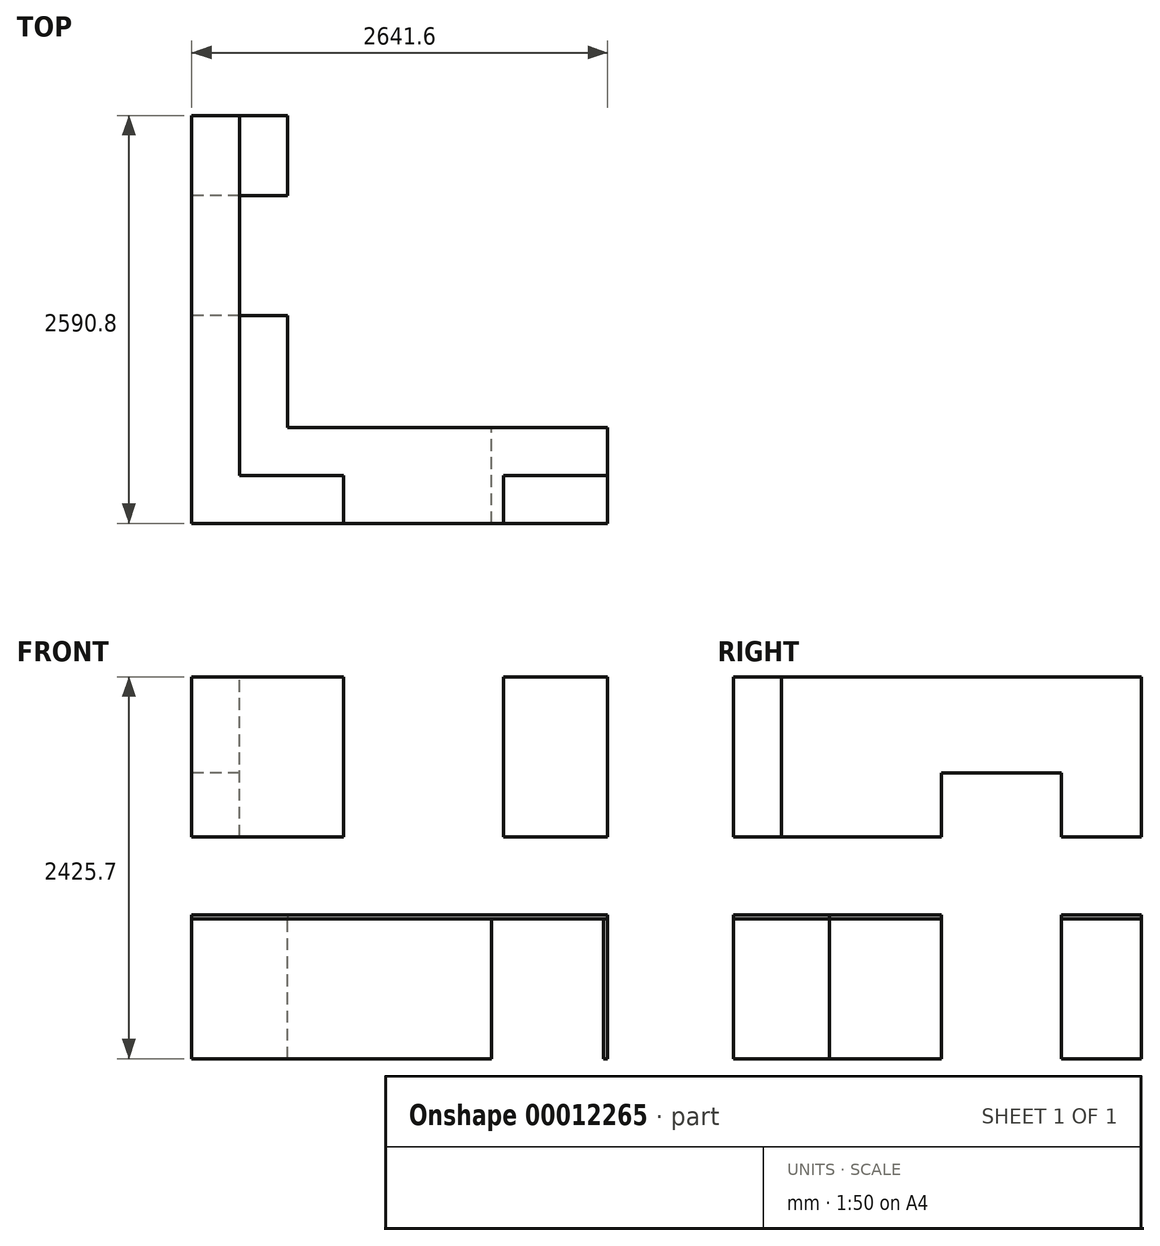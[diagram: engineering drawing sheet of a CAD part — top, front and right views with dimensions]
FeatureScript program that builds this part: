
annotation { "Feature Type Name" : "Feature", "Feature Type Description" : "" }
export const myFeature = defineFeature(function(context is Context, id is Id, definition is map)
    precondition{}
    {
        {
            var Q0;
            Q0=qCreatedBy(makeId("Top.planeOp"),FACE);
            cPlane(context, id + "F0", {"entities" : qUnion([Q0]), "cplaneType" : CPlaneType.OFFSET, "offset" : 889 * mm, "width" : 152.4 * mm, "height" : 152.4 * mm});
        }
        {
            var Q0;
            Q0=qCreatedBy(id+"F0.planeOp",FACE);
            cPlane(context, id + "F1", {"entities" : qUnion([Q0]), "cplaneType" : CPlaneType.OFFSET, "offset" : 25.4 * mm, "width" : 152.4 * mm, "height" : 152.4 * mm});
        }
        {
            var Q0;
            Q0=qCreatedBy(makeId("Top.planeOp"),FACE);
            cPlane(context, id + "F2", {"entities" : qUnion([Q0]), "cplaneType" : CPlaneType.OFFSET, "offset" : 2425.7 * mm, "width" : 152.4 * mm, "height" : 152.4 * mm});
        }
        {
            var Q0;
            Q0=qCreatedBy(id+"F0.planeOp",FACE);
            var sketch = newSketch(context, id + "F3", { "sketchPlane" : qUnion([Q0])});
            skLineSegment(sketch, "E0", {"start": v(0, 0) * mm, "end": v(0, 2590.8) * mm});
            skLineSegment(sketch, "E1", {"start": v(0, 0) * mm, "end": v(2641.6, 0) * mm});
            skLineSegment(sketch, "E2", {"start": v(0, 2590.8) * mm, "end": v(609.6, 2590.8) * mm});
            skLineSegment(sketch, "E3", {"start": v(609.6, 2590.8) * mm, "end": v(609.6, 609.6) * mm});
            skLineSegment(sketch, "E4", {"start": v(609.6, 609.6) * mm, "end": v(2641.6, 609.6) * mm});
            skLineSegment(sketch, "E5", {"start": v(2641.6, 609.6) * mm, "end": v(2641.6, 0) * mm});
            skLineSegment(sketch, "E6", {"start": v(2616.2, 609.6) * mm, "end": v(2616.2, 0) * mm});
            skLineSegment(sketch, "E7", {"start": v(1905, 609.6) * mm, "end": v(1905, 0) * mm});
            skLineSegment(sketch, "E8", {"start": v(609.6, 1320.8) * mm, "end": v(0, 1320.8) * mm});
            skLineSegment(sketch, "E9", {"start": v(609.6, 2082.8) * mm, "end": v(0, 2082.8) * mm});
            skSolve(sketch);
        }
        {
            var Q0;
            {var subQ1=sQuery(id+"F3.wireOp",EDGE,"E5");Q0=makeQuery(id+"F3.imprint","IMPRINT",FACE,{"disambiguationData":[TD([[makeQuery(id+"F3.imprint","IMPRINT",EDGE,{"derivedFrom":subQ1}),-1.0]])]});}
            var Q1;
            {var subQ1=sQuery(id+"F3.wireOp",EDGE,"E7");Q1=makeQuery(id+"F3.imprint","IMPRINT",FACE,{"disambiguationData":[TD([[makeQuery(id+"F3.imprint","IMPRINT",EDGE,{"derivedFrom":subQ1}),-1.0]])]});}
            var Q2;
            {var subQ2=sQuery(id+"F3.wireOp",EDGE,"E2");Q2=makeQuery(id+"F3.imprint","IMPRINT",FACE,{"disambiguationData":[TD([[makeQuery(id+"F3.imprint","IMPRINT",EDGE,{"derivedFrom":subQ2}),-1.0]])]});}
            var Q3;
            Q3=qCreatedBy(makeId("Top.planeOp"),FACE);
            extrude(context, id + "F4", {"entities" : qUnion([Q0, Q1, Q2]), "endBound" : BoundingType.UP_TO_SURFACE, "oppositeDirection" : true, "endBoundEntityFace" : qUnion([Q3]), "depth" : 25.4 * mm});
        }
        {
            var Q0;
            {var subQ1=sQuery(id+"F3.wireOp",EDGE,"E5");Q0=makeQuery(id+"F3.imprint","IMPRINT",FACE,{"disambiguationData":[TD([[makeQuery(id+"F3.imprint","IMPRINT",EDGE,{"derivedFrom":subQ1}),-1.0]])]});}
            var Q1;
            {var subQ1=sQuery(id+"F3.wireOp",EDGE,"E6");Q1=makeQuery(id+"F3.imprint","IMPRINT",FACE,{"disambiguationData":[TD([[makeQuery(id+"F3.imprint","IMPRINT",EDGE,{"derivedFrom":subQ1}),-1.0]])]});}
            var Q2;
            {var subQ1=sQuery(id+"F3.wireOp",EDGE,"E7");Q2=makeQuery(id+"F3.imprint","IMPRINT",FACE,{"disambiguationData":[TD([[makeQuery(id+"F3.imprint","IMPRINT",EDGE,{"derivedFrom":subQ1}),-1.0]])]});}
            var Q3;
            {var subQ2=sQuery(id+"F3.wireOp",EDGE,"E2");Q3=makeQuery(id+"F3.imprint","IMPRINT",FACE,{"disambiguationData":[TD([[makeQuery(id+"F3.imprint","IMPRINT",EDGE,{"derivedFrom":subQ2}),-1.0]])]});}
            var Q4;
            Q4=qCreatedBy(id+"F1.planeOp",FACE);
            extrude(context, id + "F5", {"entities" : qUnion([Q0, Q1, Q2, Q3]), "endBound" : BoundingType.UP_TO_SURFACE, "endBoundEntityFace" : qUnion([Q4]), "depth" : 25.4 * mm});
        }
        {
            var Q0;
            Q0=qCreatedBy(id+"F2.planeOp",FACE);
            var sketch = newSketch(context, id + "F6", { "sketchPlane" : qUnion([Q0])});
            skLineSegment(sketch, "E10", {"start": v(0, 0) * mm, "end": v(0, 2590.8) * mm});
            skLineSegment(sketch, "E11", {"start": v(0, 0) * mm, "end": v(2641.6, 0) * mm});
            skLineSegment(sketch, "E12", {"start": v(0, 2590.8) * mm, "end": v(304.8, 2590.8) * mm});
            skLineSegment(sketch, "E13", {"start": v(304.8, 2590.8) * mm, "end": v(304.8, 304.8) * mm});
            skLineSegment(sketch, "E14", {"start": v(304.8, 304.8) * mm, "end": v(965.2, 304.8) * mm});
            skLineSegment(sketch, "E15", {"start": v(965.2, 304.8) * mm, "end": v(965.2, 0) * mm});
            skLineSegment(sketch, "E16", {"start": v(1981.2, 0) * mm, "end": v(1981.2, 304.8) * mm});
            skLineSegment(sketch, "E17", {"start": v(1981.2, 304.8) * mm, "end": v(2641.6, 304.8) * mm});
            skLineSegment(sketch, "E18", {"start": v(2641.6, 304.8) * mm, "end": v(2641.6, 0) * mm});
            skLineSegment(sketch, "E19", {"start": v(304.8, 2082.8) * mm, "end": v(0, 2082.8) * mm});
            skLineSegment(sketch, "E20", {"start": v(304.8, 1320.8) * mm, "end": v(0, 1320.8) * mm});
            skSolve(sketch);
        }
        {
            var Q0;
            {var subQ1=sQuery(id+"F6.wireOp",EDGE,"E16");Q0=makeQuery(id+"F6.imprint","IMPRINT",FACE,{"disambiguationData":[TD([[makeQuery(id+"F6.imprint","IMPRINT",EDGE,{"derivedFrom":subQ1}),-1.0]])]});}
            var Q1;
            {var subQ2=sQuery(id+"F6.wireOp",EDGE,"E14");Q1=makeQuery(id+"F6.imprint","IMPRINT",FACE,{"disambiguationData":[TD([[makeQuery(id+"F6.imprint","IMPRINT",EDGE,{"derivedFrom":subQ2}),-1.0]])]});}
            var Q2;
            {var subQ1=sQuery(id+"F6.wireOp",EDGE,"E19");Q2=makeQuery(id+"F6.imprint","IMPRINT",FACE,{"disambiguationData":[TD([[makeQuery(id+"F6.imprint","IMPRINT",EDGE,{"derivedFrom":subQ1}),1.0]])]});}
            var Q3;
            {var subQ2=sQuery(id+"F6.wireOp",EDGE,"E12");Q3=makeQuery(id+"F6.imprint","IMPRINT",FACE,{"disambiguationData":[TD([[makeQuery(id+"F6.imprint","IMPRINT",EDGE,{"derivedFrom":subQ2}),-1.0]])]});}
            extrude(context, id + "F7", {"entities" : qUnion([Q0, Q1, Q2, Q3]), "oppositeDirection" : true, "depth" : 1016 * mm});
        }
        {
            var Q0;
            {var subQ1=sQuery(id+"F6.wireOp",EDGE,"E19");Q0=makeQuery(id+"F6.imprint","IMPRINT",FACE,{"disambiguationData":[TD([[makeQuery(id+"F6.imprint","IMPRINT",EDGE,{"derivedFrom":subQ1}),1.0]])]});}
            extrude(context, id + "F8", {"entities" : qUnion([Q0]), "operationType" : NewBodyOperationType.REMOVE, "oppositeDirection" : true, "depth" : 1270 * mm, "hasSecondDirection" : true, "secondDirectionOppositeDirection" : true, "secondDirectionDepth" : 609.6 * mm});
        }
    });
